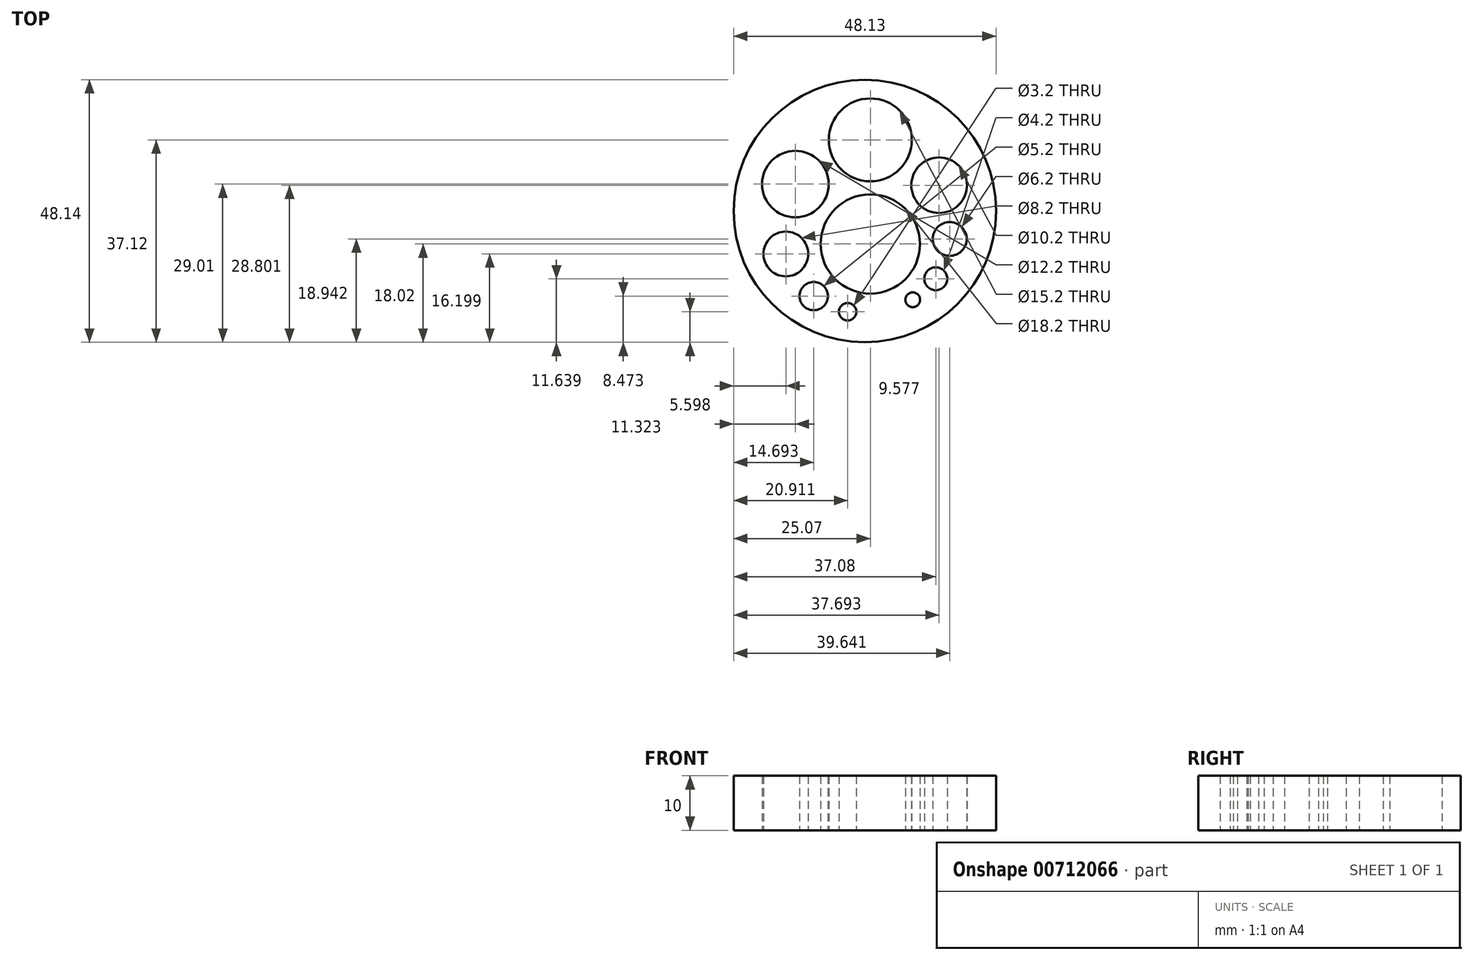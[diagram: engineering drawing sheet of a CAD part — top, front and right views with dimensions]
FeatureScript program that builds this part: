
annotation { "Feature Type Name" : "Feature", "Feature Type Description" : "" }
export const myFeature = defineFeature(function(context is Context, id is Id, definition is map)
    precondition{}
    {
        {
            var Q0;
            Q0=qCreatedBy(makeId("Top.planeOp"),FACE);
            var sketch = newSketch(context, id + "F0", { "sketchPlane" : qUnion([Q0])});
            skCircle(sketch, "E0", {"center": v(0, 0) * mm, "radius": 9.1 * mm});
            skCircle(sketch, "E1", {"center": v(0, 19.1) * mm, "radius": 7.6 * mm});
            skCircle(sketch, "E2", {"center": v(-13.75, 10.99) * mm, "radius": 6.1 * mm});
            skCircle(sketch, "E3", {"center": v(12.62, 10.78) * mm, "radius": 5.1 * mm});
            skCircle(sketch, "E4", {"center": v(-15.5, -1.82) * mm, "radius": 4.1 * mm});
            skCircle(sketch, "E5", {"center": v(14.57, 0.92) * mm, "radius": 3.1 * mm});
            skCircle(sketch, "E6", {"center": v(-10.38, -9.55) * mm, "radius": 2.6 * mm});
            skCircle(sketch, "E7", {"center": v(12.01, -6.38) * mm, "radius": 2.1 * mm});
            skCircle(sketch, "E8", {"center": v(-4.16, -12.42) * mm, "radius": 1.6 * mm});
            skCircle(sketch, "E9", {"center": v(7.79, -10.22) * mm, "radius": 1.35 * mm});
            skCircle(sketch, "E10", {"center": v(0, 0) * mm, "radius": 11.5 * mm, "construction": true});
            skCircle(sketch, "E11", {"center": v(-1, 6.05) * mm, "radius": 24.07 * mm});
            skSolve(sketch);
        }
        {
            var Q0;
            Q0=makeQuery(id+"F0.imprint","IMPRINT",FACE,{"disambiguationData":[TD([[makeQuery(id+"F0.imprint","IMPRINT",EDGE,{"derivedFrom":sQuery(id+"F0.wireOp",EDGE,"E0")}),-1.0]])]});
            extrude(context, id + "F1", {"entities" : qUnion([Q0]), "depth" : 10 * mm, "offsetDistance" : 25 * mm});
        }
    });
